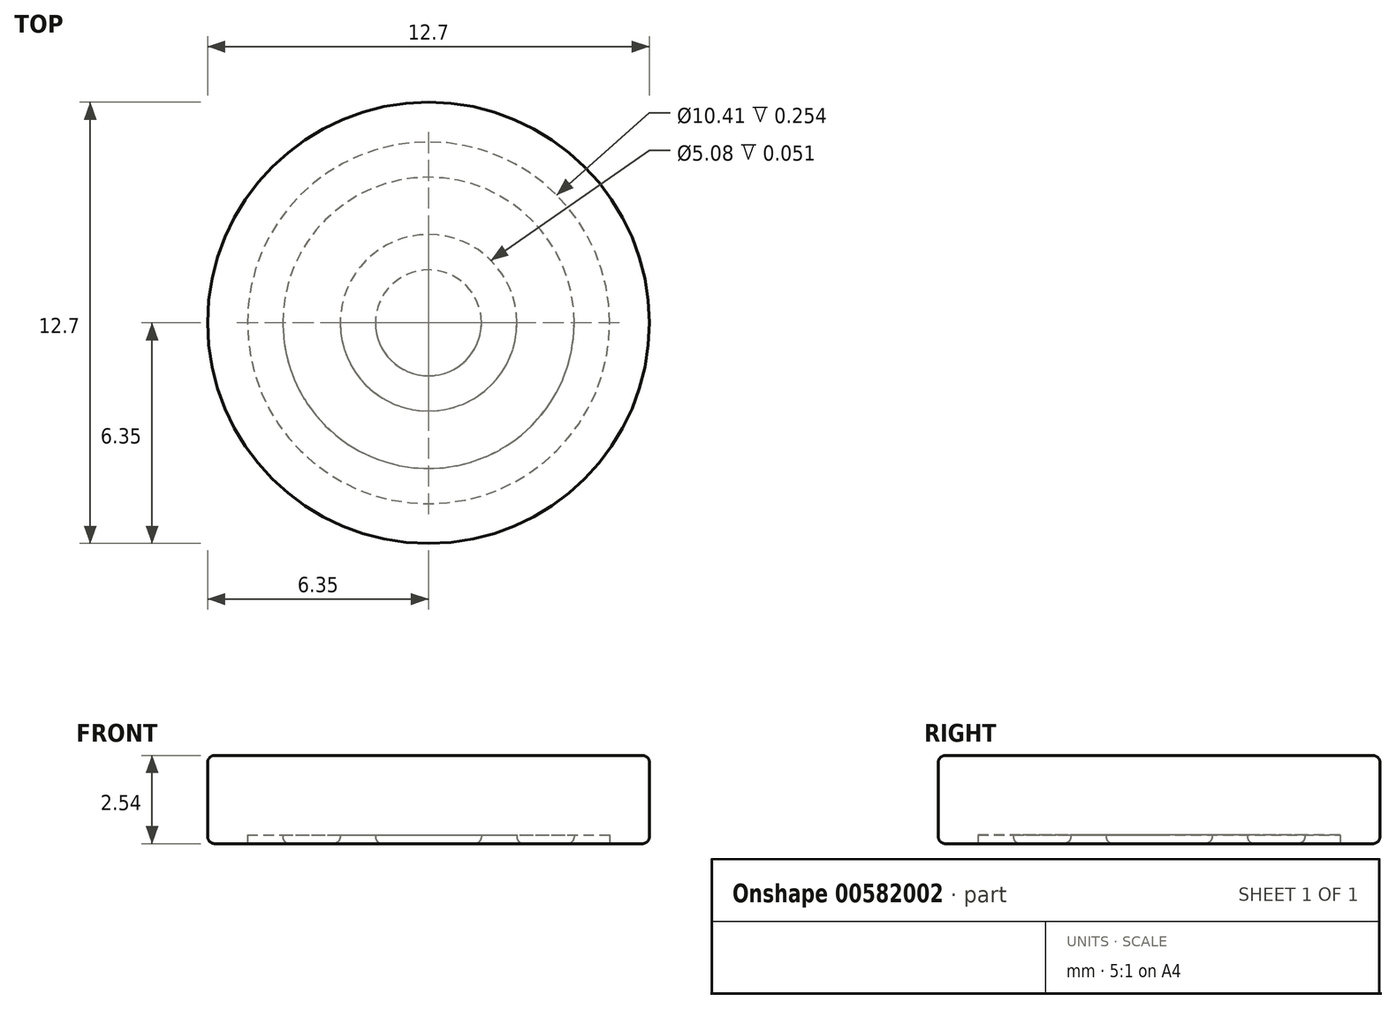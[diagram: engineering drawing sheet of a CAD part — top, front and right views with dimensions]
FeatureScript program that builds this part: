
annotation { "Feature Type Name" : "Feature", "Feature Type Description" : "" }
export const myFeature = defineFeature(function(context is Context, id is Id, definition is map)
    precondition{}
    {
        {
            var Q0;
            Q0=qCreatedBy(makeId("Top.planeOp"),FACE);
            var sketch = newSketch(context, id + "F0", { "sketchPlane" : qUnion([Q0])});
            skCircle(sketch, "E0", {"center": v(0, 0) * mm, "radius": 6.35 * mm});
            skSolve(sketch);
        }
        {
            var Q0;
            Q0=makeQuery(id+"F0.imprint","IMPRINT",FACE,{"disambiguationData":[TD([[makeQuery(id+"F0.imprint","IMPRINT",EDGE,{"derivedFrom":sQuery(id+"F0.wireOp",EDGE,"E0")}),1.0]])]});
            extrude(context, id + "F1", {"entities" : qUnion([Q0]), "endBound" : BoundingType.SYMMETRIC, "depth" : 2.54 * mm, "offsetDistance" : 25.4 * mm});
        }
        {
            var Q0;
            Q0=makeQuery(id+"F1.opExtrude","CAP_EDGE",EDGE,{"disambiguationData":[OSD([sQuery(id+"F0.wireOp",EDGE,"E0")])],"isStart":true});
            var Q1;
            Q1=makeQuery(id+"F1.opExtrude","CAP_EDGE",EDGE,{"disambiguationData":[OSD([sQuery(id+"F0.wireOp",EDGE,"E0")])],"isStart":false});
            fillet(context, id + "F2", {"entities" : qUnion([Q0, Q1]), "radius" : 0.2 * mm, "tangentPropagation" : true, "allowEdgeOverflow" : false});
        }
        {
            var Q0;
            Q0=makeQuery(id+"F1.opExtrude","CAP_FACE",FACE,{"disambiguationData":[OSD([sQuery(id+"F0.wireOp",EDGE,"E0")])],"isStart":true});
            var sketch = newSketch(context, id + "F3", { "sketchPlane" : qUnion([Q0])});
            skCircle(sketch, "E1", {"center": v(0, 0) * mm, "radius": 1.52 * mm});
            skCircle(sketch, "E2", {"center": v(0, 0) * mm, "radius": 2.54 * mm});
            skCircle(sketch, "E3", {"center": v(0, 0) * mm, "radius": 4.2 * mm});
            skCircle(sketch, "E4", {"center": v(0, 0) * mm, "radius": 5.2 * mm});
            skSolve(sketch);
        }
        {
            var Q0;
            Q0=makeQuery(id+"F3.imprint","IMPRINT",FACE,{"disambiguationData":[TD([[makeQuery(id+"F3.imprint","IMPRINT",EDGE,{"derivedFrom":sQuery(id+"F3.wireOp",EDGE,"E1")}),-1.0]])]});
            var Q1;
            Q1=makeQuery(id+"F3.imprint","IMPRINT",FACE,{"disambiguationData":[TD([[makeQuery(id+"F3.imprint","IMPRINT",EDGE,{"derivedFrom":sQuery(id+"F3.wireOp",EDGE,"E3")}),-1.0]])]});
            extrude(context, id + "F4", {"entities" : qUnion([Q0, Q1]), "operationType" : NewBodyOperationType.REMOVE, "oppositeDirection" : true, "depth" : 0.25 * mm, "offsetDistance" : 25.4 * mm});
        }
        {
            var Q0;
            Q0=makeQuery(id+"F4.boolean.opBoolean","COPY",EDGE,{"derivedFrom":makeQuery(id+"F4.opExtrude","CAP_EDGE",EDGE,{"disambiguationData":[OSD([sQuery(id+"F3.wireOp",EDGE,"E4")])],"isStart":true})});
            var Q1;
            Q1=makeQuery(id+"F4.boolean.opBoolean","COPY",EDGE,{"derivedFrom":makeQuery(id+"F4.opExtrude","CAP_EDGE",EDGE,{"disambiguationData":[OSD([sQuery(id+"F3.wireOp",EDGE,"E3")])],"isStart":true})});
            var Q2;
            Q2=makeQuery(id+"F4.boolean.opBoolean","COPY",EDGE,{"derivedFrom":makeQuery(id+"F4.opExtrude","CAP_EDGE",EDGE,{"disambiguationData":[OSD([sQuery(id+"F3.wireOp",EDGE,"E2")])],"isStart":true})});
            var Q3;
            Q3=makeQuery(id+"F4.boolean.opBoolean","COPY",EDGE,{"derivedFrom":makeQuery(id+"F4.opExtrude","CAP_EDGE",EDGE,{"disambiguationData":[OSD([sQuery(id+"F3.wireOp",EDGE,"E1")])],"isStart":true})});
            fillet(context, id + "F5", {"entities" : qUnion([Q0, Q1, Q2, Q3]), "radius" : 0.2 * mm, "tangentPropagation" : true, "allowEdgeOverflow" : false});
        }
    });
